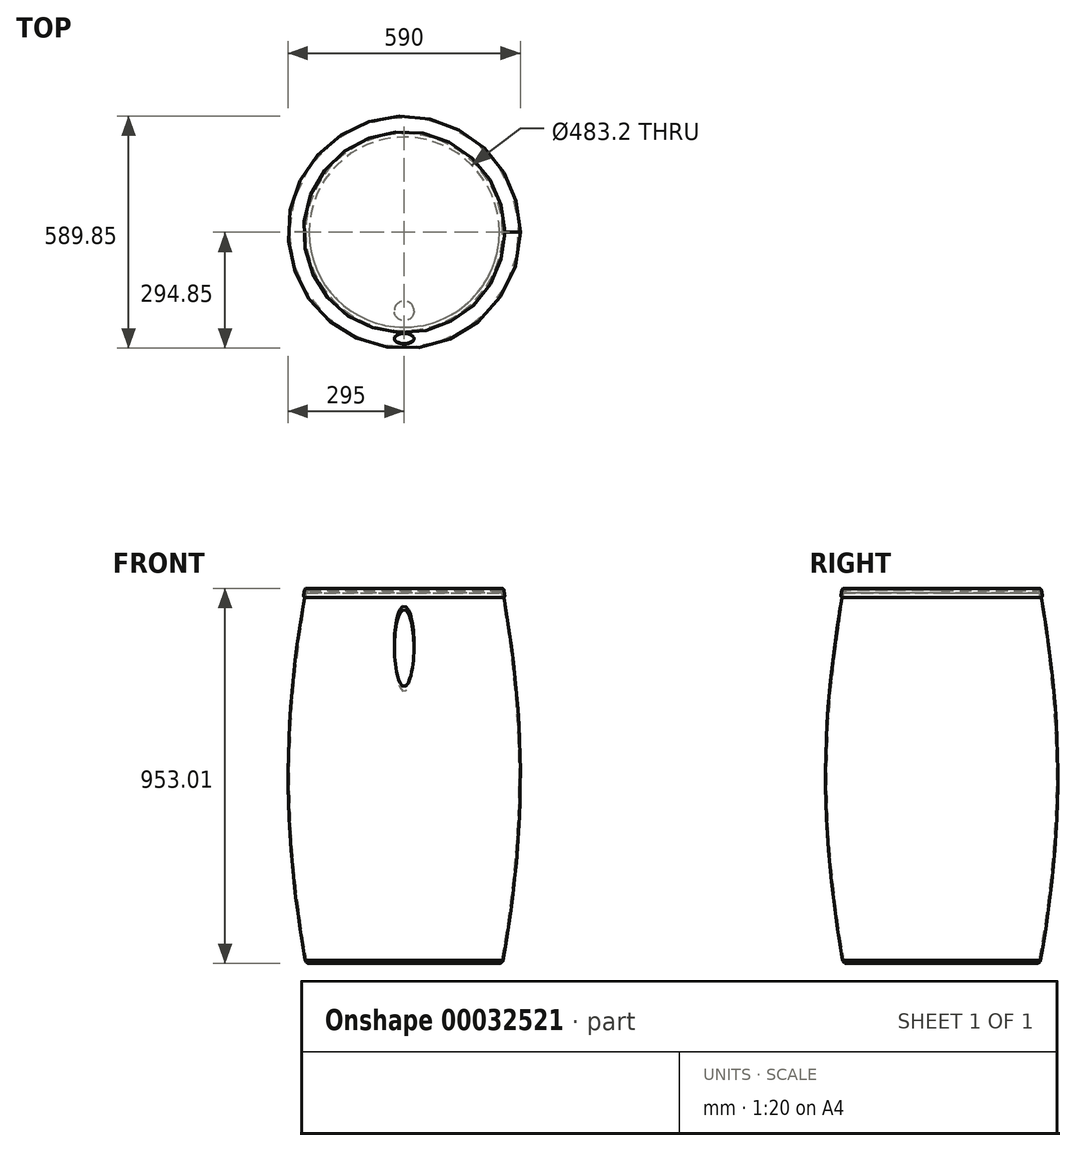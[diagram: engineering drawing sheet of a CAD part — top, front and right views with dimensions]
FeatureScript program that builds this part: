
annotation { "Feature Type Name" : "Feature", "Feature Type Description" : "" }
export const myFeature = defineFeature(function(context is Context, id is Id, definition is map)
    precondition{}
    {
        {
            var Q0;
            Q0=qCreatedBy(makeId("Front.planeOp"),FACE);
            var sketch = newSketch(context, id + "F0", { "sketchPlane" : qUnion([Q0])});
            skLineSegment(sketch, "E0", {"start": v(0, 0) * mm, "end": v(-250, 0) * mm});
            skLineSegment(sketch, "E1", {"start": v(0, 950) * mm, "end": v(-250, 950) * mm});
            skLineSegment(sketch, "E2", {"start": v(-250, 950) * mm, "end": v(-250, 0) * mm, "construction": true});
            skFitSpline(sketch, "E3", {"points": [v(-250, 950) * mm, v(-250, 0) * mm], "startDerivative": vector(-180, -1020.83) * mm, "endDerivative": vector(180, -1020.83) * mm});
            skLineSegment(sketch, "E4", {"start": v(-250, 950) * mm, "end": v(-241.27, 999.53) * mm, "construction": true});
            skLineSegment(sketch, "E5", {"start": v(-250, 0) * mm, "end": v(-236.95, -74.03) * mm, "construction": true});
            skLineSegment(sketch, "E6", {"start": v(0, 950) * mm, "end": v(0, 0) * mm});
            skSolve(sketch);
        }
        {
            var Q0;
            Q0=makeQuery(id+"F0.imprint","IMPRINT",FACE,{"disambiguationData":[TD([[makeQuery(id+"F0.imprint","IMPRINT",EDGE,{"derivedFrom":sQuery(id+"F0.wireOp",EDGE,"E0")}),-1.0]])]});
            var Q1;
            Q1=sQuery(id+"F0.wireOp",EDGE,"E6");
            revolve(context, id + "F1", {"entities" : qUnion([Q0]), "axis" : qUnion([Q1]), "revolveType" : RevolveType.FULL});
        }
        {
            var Q0;
            Q0=makeQuery(id+"F1.opRevolve","SWEPT_EDGE",EDGE,{"disambiguationData":[OSD([sQuery(id+"F0.wireOp",EDGE,"E1"),sQuery(id+"F0.wireOp",EDGE,"E3")])]});
            var Q1;
            Q1=makeQuery(id+"F1.opRevolve","SWEPT_EDGE",EDGE,{"disambiguationData":[OSD([sQuery(id+"F0.wireOp",EDGE,"E0"),sQuery(id+"F0.wireOp",EDGE,"E3")])]});
            fillet(context, id + "F2", {"entities" : qUnion([Q0, Q1]), "radius" : 10 * mm, "tangentPropagation" : true, "allowEdgeOverflow" : false});
        }
        {
            var Q0;
            Q0=makeQuery(id+"F1.opRevolve","SWEPT_FACE",FACE,{"disambiguationData":[OSD([sQuery(id+"F0.wireOp",EDGE,"E1")])]});
            shell(context, id + "F3", {"entities" : qUnion([Q0]), "thickness" : 2.5 * mm});
        }
        {
            var Q0;
            Q0=makeQuery(id+"F3.opShell","OFFSET_FACE",FACE,{"disambiguationData":[OSD([sQuery(id+"F0.wireOp",EDGE,"E0")])]});
            var sketch = newSketch(context, id + "F4", { "sketchPlane" : qUnion([Q0])});
            skCircle(sketch, "E7", {"center": v(0, -200) * mm, "radius": 15 * mm});
            skLineSegment(sketch, "E8", {"start": v(0, 0) * mm, "end": v(0, -200) * mm, "construction": true});
            skSolve(sketch);
        }
        {
            var Q0;
            Q0=sQuery(id+"F4.wireOp",EDGE,"E8");
            cPlane(context, id + "F5", {"entities" : qUnion([Q0]), "cplaneType" : CPlaneType.LINE_ANGLE, "offset" : 25 * mm, "angle" : 90 * degree, "width" : 150 * mm, "height" : 150 * mm});
        }
        {
            var Q0;
            Q0=qCreatedBy(id+"F5.planeOp",FACE);
            var sketch = newSketch(context, id + "F6", { "sketchPlane" : qUnion([Q0])});
            skFitSpline(sketch, "E9", {"points": [v(-200, 0) * mm, v(-461.72, 2000) * mm], "startDerivative": vector(-99.07, 1928.72) * mm, "endDerivative": vector(-296.66, 1172.3) * mm});
            skLineSegment(sketch, "E10", {"start": v(-200, 0) * mm, "end": v(-200, 2000) * mm, "construction": true});
            skLineSegment(sketch, "E11", {"start": v(-461.72, 2000) * mm, "end": v(-200, 2000) * mm, "construction": true});
            skLineSegment(sketch, "E12", {"start": v(-200, 0) * mm, "end": v(0, 0) * mm});
            skSolve(sketch);
        }
        {
            var Q0;
            Q0=makeQuery(id+"F4.imprint","IMPRINT",FACE,{"disambiguationData":[TD([[makeQuery(id+"F4.imprint","IMPRINT",EDGE,{"derivedFrom":sQuery(id+"F4.wireOp",EDGE,"E7")}),1.0]])]});
            var Q1;
            Q1=sQuery(id+"F6.wireOp",EDGE,"E9");
            sweep(context, id + "F7", {"profiles" : qUnion([Q0]), "path" : qUnion([Q1])});
        }
        {
            var Q0;
            Q0=makeQuery(id+"F3.opShell","OFFSET_FACE",FACE,{"disambiguationData":[OSD([sQuery(id+"F0.wireOp",EDGE,"E0")])]});
            var sketch = newSketch(context, id + "F8", { "sketchPlane" : qUnion([Q0])});
            skCircle(sketch, "E13.0", {"center": v(0, -200) * mm, "radius": 15 * mm, "construction": true});
            skCircle(sketch, "E14", {"center": v(0, -200) * mm, "radius": 25 * mm});
            skSolve(sketch);
        }
        {
            var Q0;
            Q0=makeQuery(id+"F8.imprint","IMPRINT",FACE,{"disambiguationData":[TD([[makeQuery(id+"F8.imprint","IMPRINT",EDGE,{"derivedFrom":sQuery(id+"F8.wireOp",EDGE,"E14")}),1.0]])]});
            var Q1;
            Q1=sQuery(id+"F6.wireOp",EDGE,"E9");
            sweep(context, id + "F9", {"operationType" : NewBodyOperationType.REMOVE, "profiles" : qUnion([Q0]), "path" : qUnion([Q1])});
        }
        {
            var Q0;
            Q0=qCreatedBy(makeId("Front.planeOp"),FACE);
            var sketch = newSketch(context, id + "F10", { "sketchPlane" : qUnion([Q0])});
            skLineSegment(sketch, "E15.0", {"start": v(0, 950) * mm, "end": v(-250, 950) * mm});
            skLineSegment(sketch, "E16", {"start": v(-250, 950) * mm, "end": v(-253.47, 930.3) * mm});
            skLineSegment(sketch, "E17", {"start": v(-253.47, 930.3) * mm, "end": v(-256.43, 930.82) * mm});
            skLineSegment(sketch, "E18", {"start": v(-256.43, 930.82) * mm, "end": v(-252.52, 953) * mm});
            skLineSegment(sketch, "E19", {"start": v(-252.52, 953) * mm, "end": v(0, 953) * mm});
            skLineSegment(sketch, "E20", {"start": v(0, 953) * mm, "end": v(0, 950) * mm});
            skSolve(sketch);
        }
        {
            var Q0;
            Q0=makeQuery(id+"F10.imprint","IMPRINT",FACE,{"disambiguationData":[TD([[makeQuery(id+"F10.imprint","IMPRINT",EDGE,{"derivedFrom":sQuery(id+"F10.wireOp",EDGE,"E15.0")}),-1.0]])]});
            var Q1;
            Q1=sQuery(id+"F0.wireOp",EDGE,"E6");
            revolve(context, id + "F11", {"entities" : qUnion([Q0]), "axis" : qUnion([Q1]), "revolveType" : RevolveType.FULL});
        }
        {
            var Q0;
            Q0=makeQuery(id+"F11.opRevolve","SWEPT_EDGE",EDGE,{"disambiguationData":[OSD([sQuery(id+"F10.wireOp",EDGE,"E18"),sQuery(id+"F10.wireOp",EDGE,"E19")])]});
            var Q1;
            Q1=makeQuery(id+"F11.opRevolve","SWEPT_EDGE",EDGE,{"disambiguationData":[OSD([sQuery(id+"F10.wireOp",EDGE,"E17"),sQuery(id+"F10.wireOp",EDGE,"E18")])]});
            fillet(context, id + "F12", {"entities" : qUnion([Q0, Q1]), "radius" : 5 * mm, "tangentPropagation" : true, "allowEdgeOverflow" : false});
        }
    });
